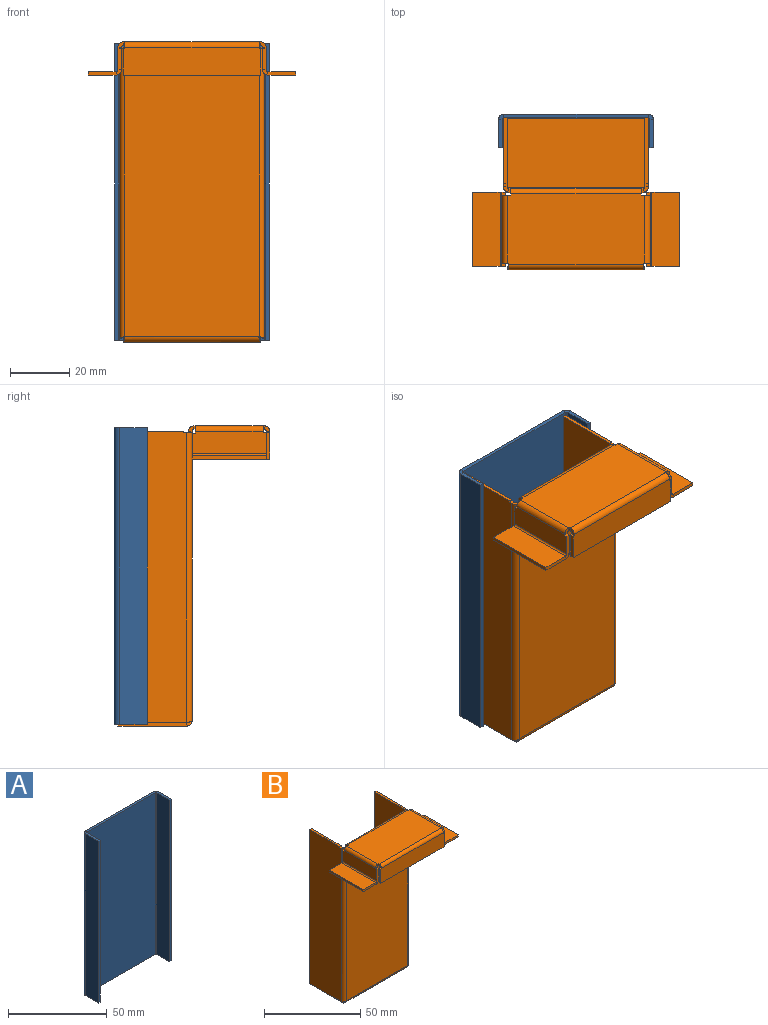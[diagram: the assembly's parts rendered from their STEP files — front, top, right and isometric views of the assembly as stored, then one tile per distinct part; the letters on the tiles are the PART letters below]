
ASSEMBLY  parts=2 mates=1
PART A: 22 faces, bbox 52.2x11.2x100 mm
  f0: plane 9.4x1.2mm, normal (0,0,1), area 11.3mm2, adj f2,f3,f4,f19
  f1: plane 9.4x1.2mm, normal (0,0,-1), area 11.3mm2, adj f2,f3,f4,f18
  f2: plane 100x1.2mm, normal (0,-1,0), area 120mm2, adj f0,f1,f3,f4
  f3: plane 100x9.4mm, normal (-1,0,0), area 940mm2, adj f0,f1,f2,f21
  f4: plane 100x9.4mm, normal (1,0,0), area 940mm2, adj f0,f1,f2,f20
  f5: plane 48.6x1.2mm, normal (0,0,1), area 58.3mm2, adj f7,f8,f15,f19
  f6: plane 48.6x1.2mm, normal (0,0,-1), area 58.3mm2, adj f7,f8,f14,f18
  f7: plane 100x48.6mm, normal (0,-1,0), area 4860mm2, adj f5,f6,f17,f21
  f8: plane 100x48.6mm, normal (0,1,0), area 4860mm2, adj f5,f6,f16,f20
  f9: plane 9.4x1.2mm, normal (0,0,1), area 11.3mm2, adj f10,f12,f13,f15
  f10: plane 100x1.2mm, normal (0,-1,0), area 120mm2, adj f9,f11,f12,f13
  f11: plane 9.4x1.2mm, normal (0,0,-1), area 11.3mm2, adj f10,f12,f13,f14
  f12: plane 100x9.4mm, normal (1,0,0), area 940mm2, adj f9,f10,f11,f17
  f13: plane 100x9.4mm, normal (-1,0,0), area 940mm2, adj f9,f10,f11,f16
  f14: plane 1.8x1.8mm, normal (0,0,-1), area 2.3mm2, adj f6,f11,f16,f17
  f15: plane 1.8x1.8mm, normal (0,0,1), area 2.3mm2, adj f5,f9,f16,f17
  f16: cylinder r=1.8mm len=100mm, axis (0,0,-1), area 282.7mm2, adj f8,f13,f14,f15
  f17: cylinder r=0.6mm len=100mm, axis (0,0,-1), area 94.2mm2, adj f7,f12,f14,f15
  f18: plane 1.8x1.8mm, normal (0,0,-1), area 2.3mm2, adj f1,f6,f20,f21
  f19: plane 1.8x1.8mm, normal (0,0,1), area 2.3mm2, adj f0,f5,f20,f21
  f20: cylinder r=1.8mm len=100mm, axis (0,0,-1), area 282.7mm2, adj f4,f8,f18,f19
  f21: cylinder r=0.6mm len=100mm, axis (0,0,-1), area 94.2mm2, adj f3,f7,f18,f19
PART B: 108 faces, bbox 70x51.2x101.2 mm
  f0: plane 9.4x1.2mm, normal (0,1,0), area 11.3mm2, adj f2,f3,f4,f105
  f1: plane 9.4x1.2mm, normal (0,-1,0), area 11.3mm2, adj f2,f3,f4,f104
  f2: plane 25x1.2mm, normal (-1,0,0), area 30mm2, adj f0,f1,f3,f4
  f3: plane 25x9.4mm, normal (0,0,-1), area 235mm2, adj f0,f1,f2,f106
  f4: plane 25x9.4mm, normal (0,0,1), area 235mm2, adj f0,f1,f2,f107
  f5: plane 7x1.2mm, normal (0,1,0), area 8.4mm2, adj f7,f8,f12,f105
  f6: plane 7.15x1.2mm, normal (0,-1,0), area 8.6mm2, adj f7,f8,f9,f104
  f7: plane 25x7.6mm, normal (1,0,0), area 188.9mm2, adj f5,f6,f9,f10,f11,f12,f99,f106
  f8: plane 25x7.6mm, normal (-1,0,0), area 188.9mm2, adj f5,f6,f9,f10,f11,f12,f98,f107
  f9: plane 1.2x1.05mm, normal (0,0,1), area 1.3mm2, adj f6,f7,f8,f10
  f10: plane 1.2x0.45mm, normal (0,-1,0), area 0.5mm2, adj f7,f8,f9,f96
  f11: plane 1.2x0.6mm, normal (0,1,0), area 0.7mm2, adj f7,f8,f12,f97
  f12: plane 1.2x1.05mm, normal (0,0,1), area 1.3mm2, adj f5,f7,f8,f11
  f13: plane 7x1.2mm, normal (0,1,0), area 8.4mm2, adj f15,f16,f17,f27
  f14: plane 7.15x1.2mm, normal (0,-1,0), area 8.6mm2, adj f15,f16,f20,f26
  f15: plane 25x7.6mm, normal (-1,0,0), area 188.9mm2, adj f13,f14,f17,f18,f19,f20,f28,f103
  f16: plane 25x7.6mm, normal (1,0,0), area 188.9mm2, adj f13,f14,f17,f18,f19,f20,f29,f102
  f17: plane 1.2x1.05mm, normal (0,0,1), area 1.3mm2, adj f13,f15,f16,f18
  f18: plane 1.2x0.6mm, normal (0,1,0), area 0.7mm2, adj f15,f16,f17,f101
  f19: plane 1.2x0.45mm, normal (0,-1,0), area 0.5mm2, adj f15,f16,f20,f100
  f20: plane 1.2x1.05mm, normal (0,0,1), area 1.3mm2, adj f14,f15,f16,f19
  f21: plane 9.4x1.2mm, normal (0,1,0), area 11.3mm2, adj f22,f24,f25,f27
  f22: plane 25x1.2mm, normal (1,0,0), area 30mm2, adj f21,f23,f24,f25
  f23: plane 9.4x1.2mm, normal (0,-1,0), area 11.3mm2, adj f22,f24,f25,f26
  f24: plane 25x9.4mm, normal (0,0,-1), area 235mm2, adj f21,f22,f23,f28
  f25: plane 25x9.4mm, normal (0,0,1), area 235mm2, adj f21,f22,f23,f29
  f26: plane 1.8x1.8mm, normal (0,-1,0), area 2.3mm2, adj f14,f23,f28,f29
  f27: plane 1.8x1.8mm, normal (0,1,0), area 2.3mm2, adj f13,f21,f28,f29
  f28: cylinder r=1.8mm len=25mm, axis (0,-1,0), area 70.7mm2, adj f15,f24,f26,f27
  f29: cylinder r=0.6mm len=25mm, axis (0,-1,0), area 23.6mm2, adj f16,f25,f26,f27
  f30: plane 46.4x23.8mm, normal (0,0,-1), area 1102.8mm2, adj f32,f33,f34,f35,f36,f37,f38,f39
  f31: plane 46.4x23.8mm, normal (0,0,1), area 1102.8mm2, adj f32,f33,f34,f35,f36,f37,f38,f39
  f32: plane 1.2x1.2mm, normal (0,1,0), area 1.4mm2, adj f30,f31,f33,f97
  f33: plane 1.2x0.45mm, normal (-1,0,0), area 0.5mm2, adj f30,f31,f32,f93
  f34: plane 1.2x1.2mm, normal (0,1,0), area 1.4mm2, adj f30,f31,f35,f101
  f35: plane 1.2x0.45mm, normal (1,0,0), area 0.5mm2, adj f30,f31,f34,f92
  f36: plane 1.2x0.45mm, normal (0,-1,0), area 0.5mm2, adj f30,f31,f37,f100
  f37: plane 1.2x0.45mm, normal (1,0,0), area 0.5mm2, adj f30,f31,f36,f50
  f38: plane 1.2x0.45mm, normal (-1,0,0), area 0.5mm2, adj f30,f31,f39,f49
  f39: plane 1.2x0.45mm, normal (0,-1,0), area 0.5mm2, adj f30,f31,f38,f96
  f40: plane 8.95x1.2mm, normal (-1,0,0), area 10.7mm2, adj f42,f43,f44,f48
  f41: plane 8.95x1.2mm, normal (1,0,0), area 10.7mm2, adj f42,f43,f44,f45
  f42: plane 46.4x9.4mm, normal (0,1,0), area 435.8mm2, adj f40,f41,f44,f45,f46,f47,f48,f52
  f43: plane 46.4x9.4mm, normal (0,-1,0), area 435.8mm2, adj f40,f41,f44,f45,f46,f47,f48,f51
  f44: plane 46.4x1.2mm, normal (0,0,-1), area 55.7mm2, adj f40,f41,f42,f43
  f45: plane 1.2x0.45mm, normal (0,0,1), area 0.5mm2, adj f41,f42,f43,f46
  f46: plane 1.2x0.45mm, normal (1,0,0), area 0.5mm2, adj f42,f43,f45,f50
  f47: plane 1.2x0.45mm, normal (-1,0,0), area 0.5mm2, adj f42,f43,f48,f49
  f48: plane 1.2x0.45mm, normal (0,0,1), area 0.5mm2, adj f40,f42,f43,f47
  f49: plane 1.8x1.8mm, normal (-1,0,0), area 2.3mm2, adj f38,f47,f51,f52
  f50: plane 1.8x1.8mm, normal (1,0,0), area 2.3mm2, adj f37,f46,f51,f52
  f51: cylinder r=1.8mm len=45.5mm, axis (-1,0,0), area 128.7mm2, adj f31,f43,f49,f50
  f52: cylinder r=0.6mm len=45.5mm, axis (-1,0,0), area 42.9mm2, adj f30,f42,f49,f50
  f53: plane 97.6x45.2mm, normal (0,-1,0), area 4411mm2, adj f55,f56,f57,f58,f59,f60,f70,f79
  f54: plane 97.6x45.2mm, normal (0,1,0), area 4411mm2, adj f55,f56,f57,f58,f59,f60,f71,f80
  f55: plane 1.2x0.07mm, normal (-0.71,0,-0.71), area 0.1mm2, adj f53,f54,f77,f88
  f56: plane 1.2x0.07mm, normal (0.71,0,-0.71), area 0.1mm2, adj f53,f54,f68,f78
  f57: plane 1.2x0.6mm, normal (0,0,1), area 0.7mm2, adj f53,f54,f58,f69
  f58: plane 1.2x0.45mm, normal (1,0,0), area 0.5mm2, adj f53,f54,f57,f92
  f59: plane 1.2x0.6mm, normal (0,0,1), area 0.7mm2, adj f53,f54,f60,f89
  f60: plane 1.2x0.45mm, normal (-1,0,0), area 0.5mm2, adj f53,f54,f59,f93
  f61: plane 22x1.2mm, normal (0,0,1), area 26.4mm2, adj f62,f63,f65,f67
  f62: plane 98.1x23.2mm, normal (1,0,0), area 2275.4mm2, adj f61,f64,f65,f66,f67,f70
  f63: plane 98.1x23.2mm, normal (-1,0,0), area 2275.4mm2, adj f61,f64,f65,f66,f67,f71
  f64: plane 23.2x1.2mm, normal (0,0,-1), area 27.8mm2, adj f62,f63,f65,f68
  f65: plane 98.1x1.2mm, normal (0,1,0), area 117.7mm2, adj f61,f62,f63,f64
  f66: plane 1.2x1.2mm, normal (0,0,1), area 1.4mm2, adj f62,f63,f67,f69
  f67: plane 1.2x0.45mm, normal (0,-1,0), area 0.5mm2, adj f61,f62,f63,f66
  f68: bspline ~1.8x1.8mm, area 2.4mm2, adj f56,f64,f70,f71
  f69: plane 1.8x1.8mm, normal (0,0,1), area 2.3mm2, adj f57,f66,f70,f71
  f70: cylinder r=1.8mm len=97.65mm, axis (0,0,1), area 275.5mm2, adj f53,f62,f68,f69
  f71: cylinder r=0.6mm len=97.65mm, axis (0,0,1), area 91.8mm2, adj f54,f63,f68,f69
  f72: plane 23.2x1.2mm, normal (1,0,0), area 27.8mm2, adj f74,f75,f76,f78
  f73: plane 23.2x1.2mm, normal (-1,0,0), area 27.8mm2, adj f74,f75,f76,f77
  f74: plane 46.2x1.2mm, normal (0,1,0), area 55.4mm2, adj f72,f73,f75,f76
  f75: plane 46.2x23.2mm, normal (0,0,-1), area 1071.8mm2, adj f72,f73,f74,f79
  f76: plane 46.2x23.2mm, normal (0,0,1), area 1071.8mm2, adj f72,f73,f74,f80
  f77: bspline ~1.8x1.8mm, area 2.4mm2, adj f55,f73,f79,f80
  f78: bspline ~1.8x1.8mm, area 2.4mm2, adj f56,f72,f79,f80
  f79: cylinder r=1.8mm len=46.2mm, axis (-1,0,0), area 129.5mm2, adj f53,f75,f77,f78
  f80: cylinder r=0.6mm len=46.2mm, axis (-1,0,0), area 43.2mm2, adj f54,f76,f77,f78
  f81: plane 22x1.2mm, normal (0,0,1), area 26.4mm2, adj f82,f83,f85,f86
  f82: plane 98.1x23.2mm, normal (-1,0,0), area 2275.4mm2, adj f81,f84,f85,f86,f87,f90
  f83: plane 98.1x23.2mm, normal (1,0,0), area 2275.4mm2, adj f81,f84,f85,f86,f87,f91
  f84: plane 23.2x1.2mm, normal (0,0,-1), area 27.8mm2, adj f82,f83,f85,f88
  f85: plane 98.1x1.2mm, normal (0,1,0), area 117.7mm2, adj f81,f82,f83,f84
  f86: plane 1.2x0.45mm, normal (0,-1,0), area 0.5mm2, adj f81,f82,f83,f87
  f87: plane 1.2x1.2mm, normal (0,0,1), area 1.4mm2, adj f82,f83,f86,f89
  f88: bspline ~1.8x1.8mm, area 2.4mm2, adj f55,f84,f90,f91
  f89: plane 1.8x1.8mm, normal (0,0,1), area 2.3mm2, adj f59,f87,f90,f91
  f90: cylinder r=1.8mm len=97.65mm, axis (0,0,1), area 275.5mm2, adj f53,f82,f88,f89
  f91: cylinder r=0.6mm len=97.65mm, axis (0,0,1), area 91.8mm2, adj f54,f83,f88,f89
  f92: plane 1.8x1.8mm, normal (1,0,0), area 2.3mm2, adj f35,f58,f94,f95
  f93: plane 1.8x1.8mm, normal (-1,0,0), area 2.3mm2, adj f33,f60,f94,f95
  f94: cylinder r=1.8mm len=44mm, axis (1,0,0), area 124.4mm2, adj f31,f54,f92,f93
  f95: cylinder r=0.6mm len=44mm, axis (1,0,0), area 41.5mm2, adj f30,f53,f92,f93
  f96: plane 1.8x1.8mm, normal (0,-1,0), area 2.3mm2, adj f10,f39,f98,f99
  f97: plane 1.8x1.8mm, normal (0,1,0), area 2.3mm2, adj f11,f32,f98,f99
  f98: cylinder r=1.8mm len=22.9mm, axis (0,-1,0), area 64.8mm2, adj f8,f31,f96,f97
  f99: cylinder r=0.6mm len=22.9mm, axis (0,-1,0), area 21.6mm2, adj f7,f30,f96,f97
  f100: plane 1.8x1.8mm, normal (0,-1,0), area 2.3mm2, adj f19,f36,f102,f103
  f101: plane 1.8x1.8mm, normal (0,1,0), area 2.3mm2, adj f18,f34,f102,f103
  f102: cylinder r=1.8mm len=22.9mm, axis (0,-1,0), area 64.8mm2, adj f16,f31,f100,f101
  f103: cylinder r=0.6mm len=22.9mm, axis (0,-1,0), area 21.6mm2, adj f15,f30,f100,f101
  f104: plane 1.8x1.8mm, normal (0,-1,0), area 2.3mm2, adj f1,f6,f106,f107
  f105: plane 1.8x1.8mm, normal (0,1,0), area 2.3mm2, adj f0,f5,f106,f107
  f106: cylinder r=1.8mm len=25mm, axis (0,-1,0), area 70.7mm2, adj f3,f7,f104,f105
  f107: cylinder r=0.6mm len=25mm, axis (0,-1,0), area 23.6mm2, adj f4,f8,f104,f105
PLACE A t=(0,-0.43,-0.61)mm
PLACE B at identity fixed
MATE slider B.f54 <-> A.f7  axis (0,1,0) through (0,13.7,-50.61)mm
